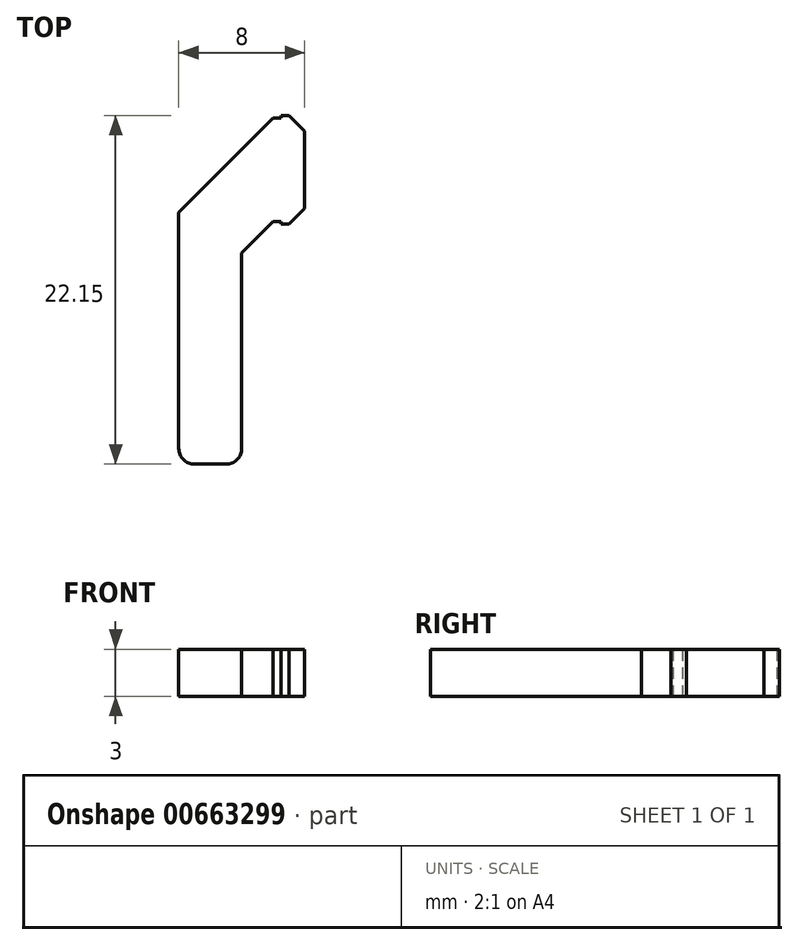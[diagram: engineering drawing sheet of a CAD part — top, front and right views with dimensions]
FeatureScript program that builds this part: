
annotation { "Feature Type Name" : "Feature", "Feature Type Description" : "" }
export const myFeature = defineFeature(function(context is Context, id is Id, definition is map)
    precondition{}
    {
        {
            var Q0;
            Q0=qCreatedBy(makeId("Top.planeOp"),FACE);
            var sketch = newSketch(context, id + "F0", { "sketchPlane" : qUnion([Q0])});
            skLineSegment(sketch, "E0", {"start": v(-4, 16) * mm, "end": v(2, 22) * mm});
            skLineSegment(sketch, "E1", {"start": v(2, 22) * mm, "end": v(4, 22) * mm});
            skLineSegment(sketch, "E2", {"start": v(4, 22) * mm, "end": v(4, 15.4) * mm});
            skLineSegment(sketch, "E3", {"start": v(4, 15.4) * mm, "end": v(2, 15.4) * mm});
            skLineSegment(sketch, "E4", {"start": v(2, 15.4) * mm, "end": v(0, 13.4) * mm});
            skLineSegment(sketch, "E5", {"start": v(0, 13.4) * mm, "end": v(0, 0) * mm});
            skLineSegment(sketch, "E6", {"start": v(0, 0) * mm, "end": v(-4, 0) * mm});
            skLineSegment(sketch, "E7", {"start": v(-4, 0) * mm, "end": v(-4, 16) * mm});
            skSolve(sketch);
        }
        {
            var Q0;
            Q0=makeQuery(id+"F0.imprint","IMPRINT",FACE,{"disambiguationData":[TD([[makeQuery(id+"F0.imprint","IMPRINT",EDGE,{"derivedFrom":sQuery(id+"F0.wireOp",EDGE,"E0")}),-1.0]])]});
            extrude(context, id + "F1", {"entities" : qUnion([Q0]), "depth" : 3 * mm, "offsetDistance" : 25 * mm});
        }
        {
            var Q0;
            Q0=makeQuery(id+"F1.opExtrude","SWEPT_FACE",FACE,{"disambiguationData":[OSD([sQuery(id+"F0.wireOp",EDGE,"E2")])]});
            var sketch = newSketch(context, id + "F2", { "sketchPlane" : qUnion([Q0])});
            skLineSegment(sketch, "E8.bottom", {"start": v(22, 3) * mm, "end": v(22.15, 3) * mm});
            skLineSegment(sketch, "E8.top", {"start": v(22, 0) * mm, "end": v(22.15, 0) * mm});
            skLineSegment(sketch, "E8.left", {"start": v(22, 3) * mm, "end": v(22, 0) * mm});
            skLineSegment(sketch, "E8.right", {"start": v(22.15, 3) * mm, "end": v(22.15, 0) * mm});
            skLineSegment(sketch, "E9.bottom", {"start": v(15.4, 3) * mm, "end": v(15.25, 3) * mm});
            skLineSegment(sketch, "E9.top", {"start": v(15.4, 0) * mm, "end": v(15.25, 0) * mm});
            skLineSegment(sketch, "E9.left", {"start": v(15.4, 3) * mm, "end": v(15.4, 0) * mm});
            skLineSegment(sketch, "E9.right", {"start": v(15.25, 3) * mm, "end": v(15.25, 0) * mm});
            skSolve(sketch);
        }
        {
            var Q0;
            Q0=makeQuery(id+"F2.imprint","IMPRINT",FACE,{"disambiguationData":[TD([[makeQuery(id+"F2.imprint","IMPRINT",EDGE,{"derivedFrom":sQuery(id+"F2.wireOp",EDGE,"E9.bottom")}),1.0]])]});
            var Q1;
            Q1=makeQuery(id+"F2.imprint","IMPRINT",FACE,{"disambiguationData":[TD([[makeQuery(id+"F2.imprint","IMPRINT",EDGE,{"derivedFrom":sQuery(id+"F2.wireOp",EDGE,"E8.bottom")}),-1.0]])]});
            extrude(context, id + "F3", {"entities" : qUnion([Q0, Q1]), "operationType" : NewBodyOperationType.ADD, "oppositeDirection" : true, "depth" : 1.5 * mm, "offsetDistance" : 25 * mm});
        }
        {
            var Q0;
            Q0=makeQuery(id+"F3.opExtrude","CAP_EDGE",EDGE,{"disambiguationData":[OSD([sQuery(id+"F2.wireOp",EDGE,"E9.right")])],"isStart":true});
            var Q1;
            Q1=makeQuery(id+"F3.opExtrude","CAP_EDGE",EDGE,{"disambiguationData":[OSD([sQuery(id+"F2.wireOp",EDGE,"E8.right")])],"isStart":true});
            chamfer(context, id + "F4", {"entities" : qUnion([Q0, Q1]), "width" : 1 * mm, "tangentPropagation" : true});
        }
        {
            var Q0;
            Q0=makeQuery(id+"F1.opExtrude","SWEPT_EDGE",EDGE,{"disambiguationData":[OSD([sQuery(id+"F0.wireOp",EDGE,"E5"),sQuery(id+"F0.wireOp",EDGE,"E6")])]});
            var Q1;
            Q1=makeQuery(id+"F1.opExtrude","SWEPT_EDGE",EDGE,{"disambiguationData":[OSD([sQuery(id+"F0.wireOp",EDGE,"E6"),sQuery(id+"F0.wireOp",EDGE,"E7")])]});
            fillet(context, id + "F5", {"entities" : qUnion([Q0, Q1]), "radius" : 1 * mm, "tangentPropagation" : true, "allowEdgeOverflow" : false});
        }
    });
